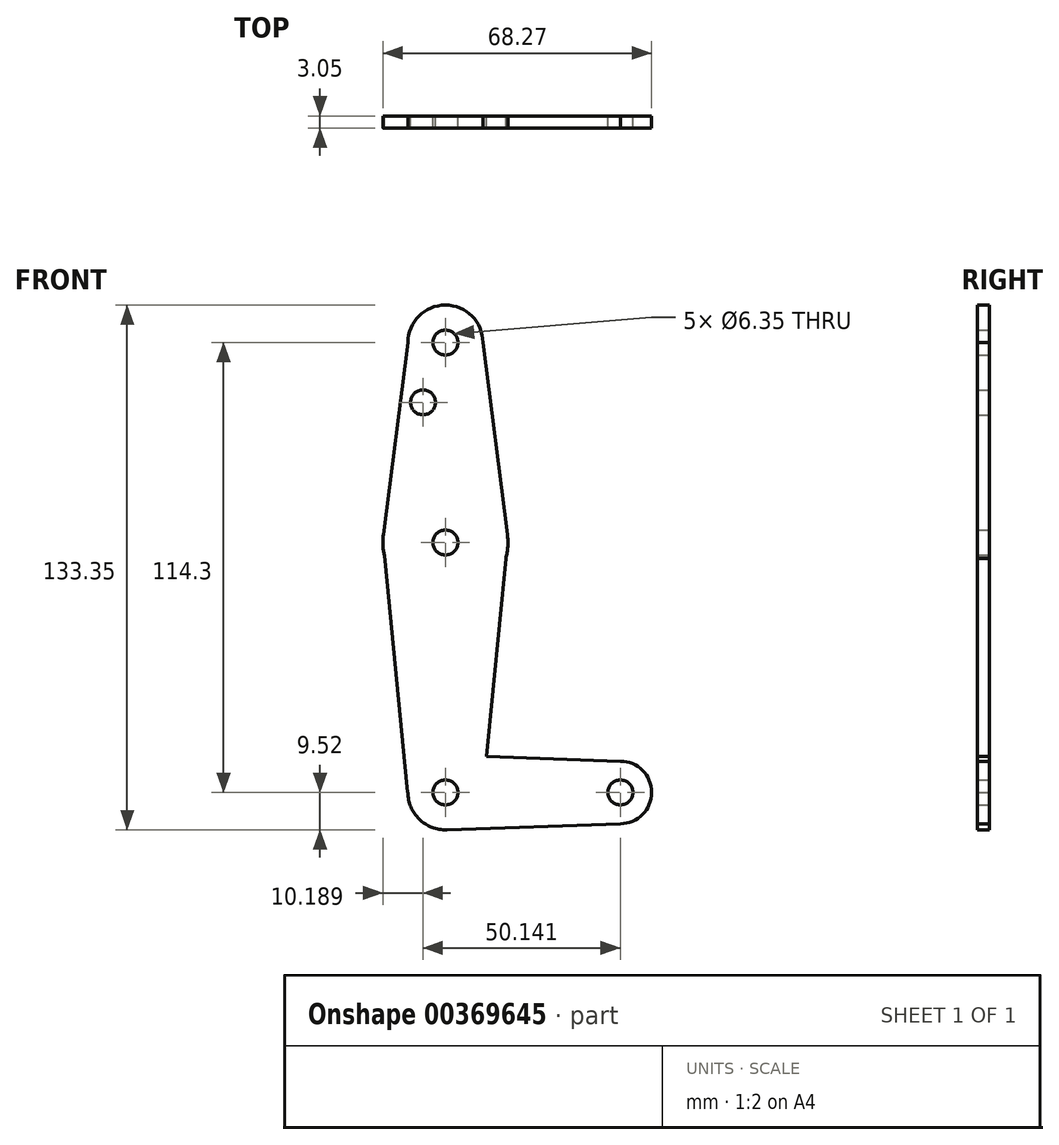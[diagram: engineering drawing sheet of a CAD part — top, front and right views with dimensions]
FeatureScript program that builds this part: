
annotation { "Feature Type Name" : "Feature", "Feature Type Description" : "" }
export const myFeature = defineFeature(function(context is Context, id is Id, definition is map)
    precondition{}
    {
        {
            var Q0;
            Q0=qCreatedBy(makeId("Front.planeOp"),FACE);
            var sketch = newSketch(context, id + "F0", { "sketchPlane" : qUnion([Q0])});
            skLineSegment(sketch, "E0", {"start": v(0, 114.3) * mm, "end": v(0, 0) * mm, "construction": true});
            skLineSegment(sketch, "E1", {"start": v(0, 0) * mm, "end": v(44.45, 0) * mm, "construction": true});
            skCircle(sketch, "E2", {"center": v(0, 114.3) * mm, "radius": 9.53 * mm});
            skCircle(sketch, "E3", {"center": v(0, 0) * mm, "radius": 9.53 * mm});
            skCircle(sketch, "E4", {"center": v(0, 63.5) * mm, "radius": 15.88 * mm});
            skLineSegment(sketch, "E5", {"start": v(9.53, 114.3) * mm, "end": v(15.75, 65.5) * mm});
            skLineSegment(sketch, "E6", {"start": v(-9.52, 114.3) * mm, "end": v(-15.75, 65.5) * mm});
            skCircle(sketch, "E7", {"center": v(44.45, 0) * mm, "radius": 7.94 * mm});
            skLineSegment(sketch, "E8", {"start": v(44.45, -7.94) * mm, "end": v(0, -9.53) * mm});
            skCircle(sketch, "E9", {"center": v(0, 0) * mm, "radius": 3.18 * mm});
            skCircle(sketch, "E10", {"center": v(44.45, 0) * mm, "radius": 3.18 * mm});
            skCircle(sketch, "E11", {"center": v(0, 114.3) * mm, "radius": 3.18 * mm});
            skCircle(sketch, "E12", {"center": v(0, 63.5) * mm, "radius": 3.18 * mm});
            skCircle(sketch, "E13", {"center": v(-5.7, 99.11) * mm, "radius": 3.18 * mm});
            skLineSegment(sketch, "E14", {"start": v(44.45, 7.94) * mm, "end": v(0, 9.53) * mm});
            skLineSegment(sketch, "E15", {"start": v(-15.87, 63.7) * mm, "end": v(-9.57, 0) * mm});
            skLineSegment(sketch, "E16", {"start": v(15.75, 63.5) * mm, "end": v(9.57, 0) * mm});
            skLineSegment(sketch, "E17", {"start": v(9.57, 0) * mm, "end": v(-9.57, 0) * mm});
            skSolve(sketch);
        }
        {
            var Q0;
            Q0 = qSketchRegion(id + "F0", true);
            extrude(context, id + "F1", {"entities" : qUnion([Q0]), "depth" : 3.05 * mm});
        }
    });
